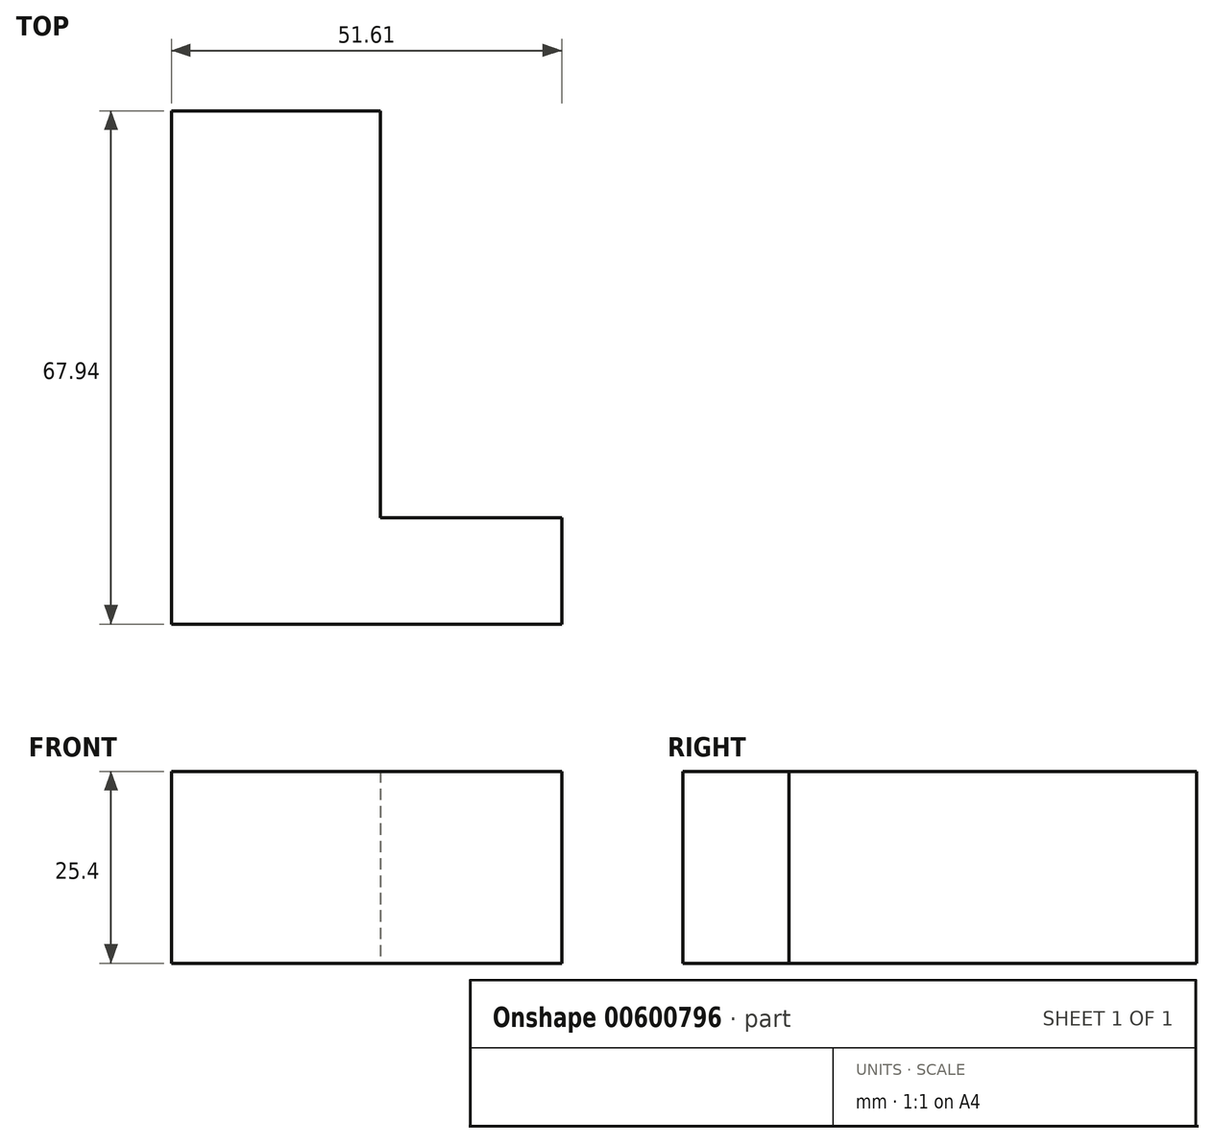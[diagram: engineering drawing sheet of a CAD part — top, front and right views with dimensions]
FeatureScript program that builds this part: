
annotation { "Feature Type Name" : "Feature", "Feature Type Description" : "" }
export const myFeature = defineFeature(function(context is Context, id is Id, definition is map)
    precondition{}
    {
        {
            var Q0;
            Q0=qCreatedBy(makeId("Top.planeOp"),FACE);
            var sketch = newSketch(context, id + "F0", { "sketchPlane" : qUnion([Q0])});
            skLineSegment(sketch, "E0.bottom", {"start": v(0, 67.94) * mm, "end": v(27.6, 67.94) * mm});
            skLineSegment(sketch, "E0.top", {"start": v(0, 0) * mm, "end": v(27.6, 0) * mm});
            skLineSegment(sketch, "E0.left", {"start": v(0, 67.94) * mm, "end": v(0, 0) * mm});
            skLineSegment(sketch, "E0.right", {"start": v(27.6, 67.94) * mm, "end": v(27.6, 0) * mm});
            skLineSegment(sketch, "E1.bottom", {"start": v(51.6, 14.07) * mm, "end": v(0, 14.07) * mm});
            skLineSegment(sketch, "E1.top", {"start": v(51.6, 0) * mm, "end": v(0, 0) * mm});
            skLineSegment(sketch, "E1.left", {"start": v(51.6, 14.07) * mm, "end": v(51.6, 0) * mm});
            skLineSegment(sketch, "E1.right", {"start": v(0, 14.07) * mm, "end": v(0, 0) * mm});
            skSolve(sketch);
        }
        {
            var Q0;
            Q0 = qSketchRegion(id + "F0", true);
            extrude(context, id + "F1", {"entities" : qUnion([Q0]), "depth" : 25.4 * mm, "offsetDistance" : 25.4 * mm});
        }
    });
